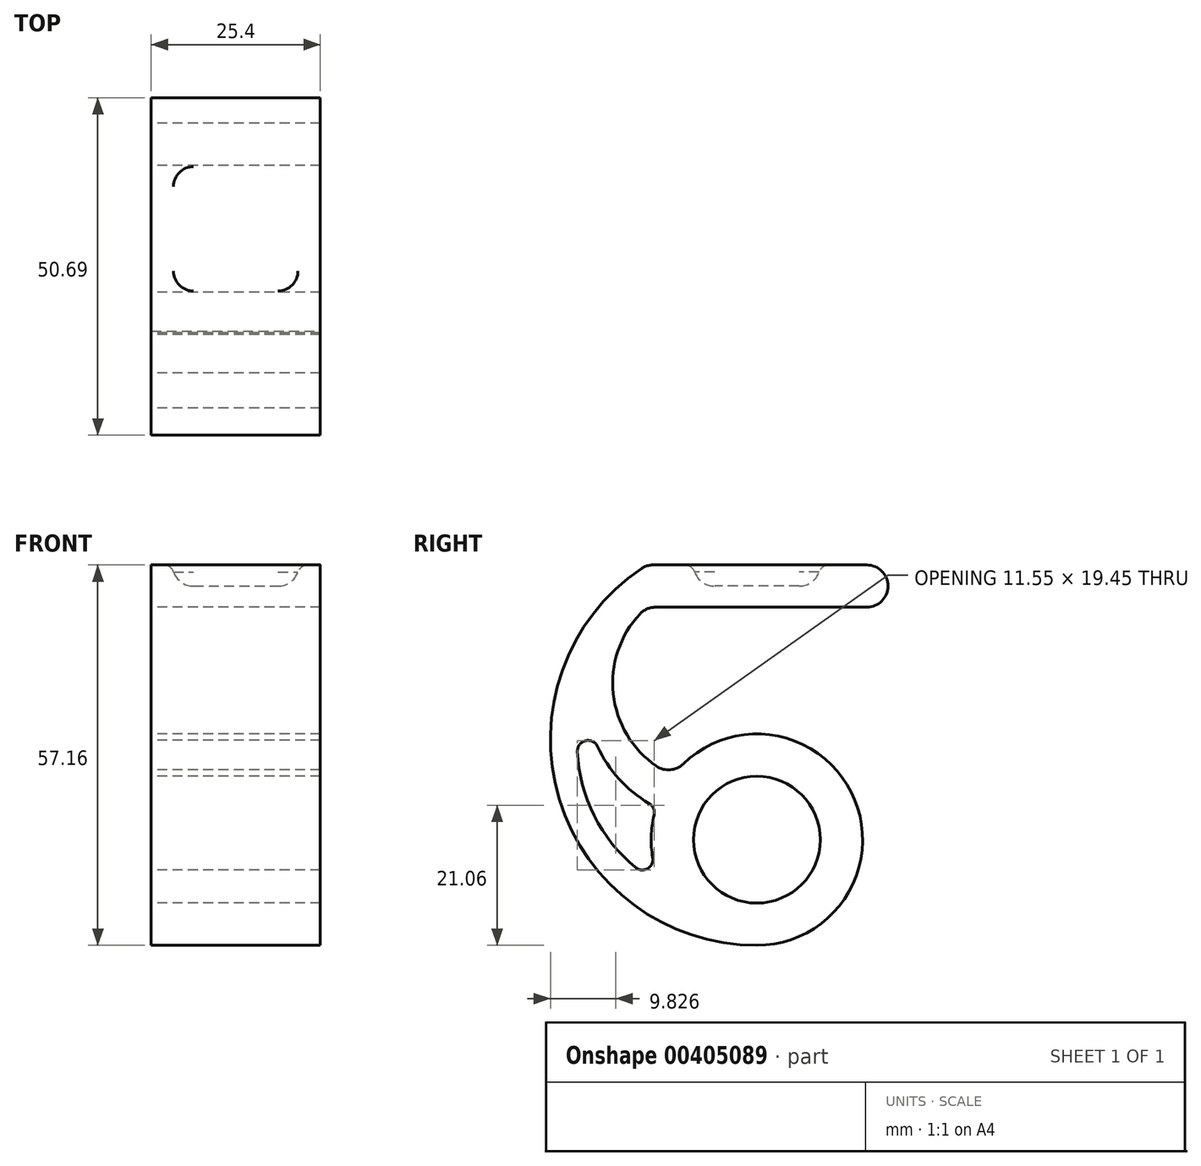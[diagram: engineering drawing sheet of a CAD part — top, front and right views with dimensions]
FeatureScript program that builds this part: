
annotation { "Feature Type Name" : "Feature", "Feature Type Description" : "" }
export const myFeature = defineFeature(function(context is Context, id is Id, definition is map)
    precondition{}
    {
        {
            var Q0;
            Q0=qCreatedBy(makeId("Right.planeOp"),FACE);
            var sketch = newSketch(context, id + "F0", { "sketchPlane" : qUnion([Q0])});
            skLineSegment(sketch, "E0.bottom", {"start": v(-16.51, 15.88) * mm, "end": v(16.51, 15.88) * mm});
            skLineSegment(sketch, "E0.top", {"start": v(-16.51, 9.53) * mm, "end": v(16.51, 9.53) * mm});
            skLineSegment(sketch, "E0.right", {"start": v(16.51, 15.88) * mm, "end": v(16.51, 9.53) * mm, "construction": true});
            skPoint(sketch, "E0.middle", {"position": v(0, 12.7) * mm});
            skLineSegment(sketch, "E1", {"start": v(-31.75, -9.53) * mm, "end": v(31.75, -9.53) * mm, "construction": true});
            skLineSegment(sketch, "E2", {"start": v(0, 9.53) * mm, "end": v(0, 0) * mm, "construction": true});
            skLineSegment(sketch, "E3", {"start": v(0, 0) * mm, "end": v(0, -9.53) * mm, "construction": true});
            skCircle(sketch, "E4", {"center": v(0, -25.4) * mm, "radius": 15.88 * mm, "construction": true});
            skArc(sketch, "E5", {"start": v(-16.51, 9.52) * mm, "mid": v(-21.47, -4.18) * mm, "end": v(-12.6, -15.74) * mm});
            skArc(sketch, "E6", {"start": v(16.51, 9.52) * mm, "mid": v(19.69, 12.7) * mm, "end": v(16.51, 15.88) * mm});
            skArc(sketch, "E7", {"start": v(-16.51, 15.87) * mm, "mid": v(-29.79, -18.92) * mm, "end": v(0, -41.28) * mm});
            skLineSegment(sketch, "E8", {"start": v(-12.6, -15.74) * mm, "end": v(0, -25.4) * mm, "construction": true});
            skLineSegment(sketch, "E9", {"start": v(0, -9.53) * mm, "end": v(0, -25.4) * mm, "construction": true});
            skArc(sketch, "E10", {"start": v(0, -41.27) * mm, "mid": v(14.24, -18.38) * mm, "end": v(-12.6, -15.74) * mm});
            skCircle(sketch, "E11", {"center": v(0, -25.4) * mm, "radius": 9.53 * mm});
            skArc(sketch, "E12", {"start": v(-25.68, -3.2) * mm, "mid": v(-22.87, -13.38) * mm, "end": v(-15.12, -20.55) * mm});
            skArc(sketch, "E13", {"start": v(-25.68, -3.2) * mm, "mid": v(-25.32, -19.77) * mm, "end": v(-14.34, -32.2) * mm});
            skArc(sketch, "E14", {"start": v(-15.12, -20.55) * mm, "mid": v(-15.84, -26.45) * mm, "end": v(-14.34, -32.2) * mm});
            skSolve(sketch);
        }
        {
            var Q0;
            Q0 = qSketchRegion(id + "F0", true);
            extrude(context, id + "F1", {"entities" : qUnion([Q0]), "depth" : 25.4 * mm, "offsetDistance" : 25.4 * mm});
        }
        {
            var Q0;
            Q0=makeQuery(id+"F1.opExtrude","SWEPT_FACE",FACE,{"disambiguationData":[OSD([sQuery(id+"F0.wireOp",EDGE,"E0.bottom")])]});
            var sketch = newSketch(context, id + "F2", { "sketchPlane" : qUnion([Q0])});
            skLineSegment(sketch, "E15.bottom", {"start": v(3.18, 9.52) * mm, "end": v(22.23, 9.53) * mm});
            skLineSegment(sketch, "E15.top", {"start": v(3.18, -9.53) * mm, "end": v(22.23, -9.53) * mm});
            skLineSegment(sketch, "E15.left", {"start": v(3.18, 9.52) * mm, "end": v(3.18, -9.53) * mm});
            skLineSegment(sketch, "E15.right", {"start": v(22.23, 9.53) * mm, "end": v(22.23, -9.52) * mm});
            skPoint(sketch, "E15.middle", {"position": v(12.7, 0) * mm});
            skLineSegment(sketch, "E16", {"start": v(12.7, 16.51) * mm, "end": v(12.7, 0) * mm, "construction": true});
            skSolve(sketch);
        }
        {
            var Q0;
            Q0 = qSketchRegion(id + "F2", true);
            extrude(context, id + "F3", {"entities" : qUnion([Q0]), "operationType" : NewBodyOperationType.REMOVE, "oppositeDirection" : true, "depth" : 3.17 * mm, "offsetDistance" : 25.4 * mm});
        }
        {
            var Q0;
            Q0=makeQuery(id+"F1.opExtrude","SWEPT_EDGE",EDGE,{"disambiguationData":[OSD([sQuery(id+"F0.wireOp",EDGE,"E5"),sQuery(id+"F0.wireOp",EDGE,"SAfVAtWe-y4kB-1YMZ-6q3z-Nys7H7JM4cN9")])]});
            var Q1;
            Q1=makeQuery(id+"F3.boolean.opBoolean","COPY",FACE,{"derivedFrom":makeQuery(id+"F3.opExtrude","CAP_FACE",FACE,{"disambiguationData":[OSD([sQuery(id+"F2.wireOp",EDGE,"E15.bottom"),sQuery(id+"F2.wireOp",EDGE,"E15.top"),sQuery(id+"F2.wireOp",EDGE,"E15.left"),sQuery(id+"F2.wireOp",EDGE,"E15.right")])],"isStart":false})});
            var Q2;
            Q2=makeQuery(id+"F3.boolean.opBoolean","COPY",EDGE,{"derivedFrom":makeQuery(id+"F3.opExtrude","SWEPT_EDGE",EDGE,{"disambiguationData":[OSD([sQuery(id+"F2.wireOp",EDGE,"E15.bottom"),sQuery(id+"F2.wireOp",EDGE,"E15.left")])]})});
            var Q3;
            Q3=makeQuery(id+"F3.boolean.opBoolean","COPY",EDGE,{"derivedFrom":makeQuery(id+"F3.opExtrude","SWEPT_EDGE",EDGE,{"disambiguationData":[OSD([sQuery(id+"F2.wireOp",EDGE,"E15.top"),sQuery(id+"F2.wireOp",EDGE,"E15.left")])]})});
            var Q4;
            Q4=makeQuery(id+"F3.boolean.opBoolean","COPY",EDGE,{"derivedFrom":makeQuery(id+"F3.opExtrude","SWEPT_EDGE",EDGE,{"disambiguationData":[OSD([sQuery(id+"F2.wireOp",EDGE,"E15.top"),sQuery(id+"F2.wireOp",EDGE,"E15.right")])]})});
            var Q5;
            Q5=makeQuery(id+"F3.boolean.opBoolean","COPY",EDGE,{"derivedFrom":makeQuery(id+"F3.opExtrude","SWEPT_EDGE",EDGE,{"disambiguationData":[OSD([sQuery(id+"F2.wireOp",EDGE,"E15.bottom"),sQuery(id+"F2.wireOp",EDGE,"E15.right")])]})});
            var Q6;
            Q6=makeQuery(id+"F1.opExtrude","SWEPT_EDGE",EDGE,{"disambiguationData":[OSD([sQuery(id+"F0.wireOp",EDGE,"E0.bottom"),sQuery(id+"F0.wireOp",EDGE,"E7")])]});
            fillet(context, id + "F4", {"entities" : qUnion([Q0, Q1, Q2, Q3, Q4, Q5, Q6]), "radius" : 3.17 * mm, "tangentPropagation" : true, "allowEdgeOverflow" : false});
        }
        {
            var Q0;
            Q0=makeQuery(id+"F4.opFillet","BLEND_EDGE",EDGE,{"blendedFrom":[makeQuery(id+"F3.boolean.opBoolean","COPY",EDGE,{"derivedFrom":makeQuery(id+"F3.opExtrude","CAP_EDGE",EDGE,{"disambiguationData":[OSD([sQuery(id+"F2.wireOp",EDGE,"E15.top")])],"isStart":false})}),makeQuery(id+"F1.opExtrude","SWEPT_FACE",FACE,{"disambiguationData":[OSD([sQuery(id+"F0.wireOp",EDGE,"E0.bottom")])]})],"blendedInto":[makeQuery(id+"F1.opExtrude","SWEPT_FACE",FACE,{"disambiguationData":[OSD([sQuery(id+"F0.wireOp",EDGE,"E0.bottom")])]})]});
            var Q1;
            Q1=makeQuery(id+"F4.opFillet","BLEND_EDGE",EDGE,{"blendedFrom":[makeQuery(id+"F3.boolean.opBoolean","COPY",VERTEX,{"derivedFrom":makeQuery(id+"F3.opExtrude","CAP_VERTEX",VERTEX,{"disambiguationData":[OSD([sQuery(id+"F2.wireOp",EDGE,"E15.top"),sQuery(id+"F2.wireOp",EDGE,"E15.left")])],"isStart":false})}),makeQuery(id+"F1.opExtrude","SWEPT_FACE",FACE,{"disambiguationData":[OSD([sQuery(id+"F0.wireOp",EDGE,"E0.bottom")])]})],"blendedInto":[makeQuery(id+"F1.opExtrude","SWEPT_FACE",FACE,{"disambiguationData":[OSD([sQuery(id+"F0.wireOp",EDGE,"E0.bottom")])]})]});
            var Q2;
            Q2=makeQuery(id+"F4.opFillet","BLEND_EDGE",EDGE,{"blendedFrom":[makeQuery(id+"F3.boolean.opBoolean","COPY",EDGE,{"derivedFrom":makeQuery(id+"F3.opExtrude","CAP_EDGE",EDGE,{"disambiguationData":[OSD([sQuery(id+"F2.wireOp",EDGE,"E15.left")])],"isStart":false})}),makeQuery(id+"F1.opExtrude","SWEPT_FACE",FACE,{"disambiguationData":[OSD([sQuery(id+"F0.wireOp",EDGE,"E0.bottom")])]})],"blendedInto":[makeQuery(id+"F1.opExtrude","SWEPT_FACE",FACE,{"disambiguationData":[OSD([sQuery(id+"F0.wireOp",EDGE,"E0.bottom")])]})]});
            var Q3;
            Q3=makeQuery(id+"F4.opFillet","BLEND_EDGE",EDGE,{"blendedFrom":[makeQuery(id+"F3.boolean.opBoolean","COPY",VERTEX,{"derivedFrom":makeQuery(id+"F3.opExtrude","CAP_VERTEX",VERTEX,{"disambiguationData":[OSD([sQuery(id+"F2.wireOp",EDGE,"E15.bottom"),sQuery(id+"F2.wireOp",EDGE,"E15.left")])],"isStart":false})}),makeQuery(id+"F1.opExtrude","SWEPT_FACE",FACE,{"disambiguationData":[OSD([sQuery(id+"F0.wireOp",EDGE,"E0.bottom")])]})],"blendedInto":[makeQuery(id+"F1.opExtrude","SWEPT_FACE",FACE,{"disambiguationData":[OSD([sQuery(id+"F0.wireOp",EDGE,"E0.bottom")])]})]});
            var Q4;
            Q4=makeQuery(id+"F4.opFillet","BLEND_EDGE",EDGE,{"blendedFrom":[makeQuery(id+"F3.boolean.opBoolean","COPY",EDGE,{"derivedFrom":makeQuery(id+"F3.opExtrude","CAP_EDGE",EDGE,{"disambiguationData":[OSD([sQuery(id+"F2.wireOp",EDGE,"E15.bottom")])],"isStart":false})}),makeQuery(id+"F1.opExtrude","SWEPT_FACE",FACE,{"disambiguationData":[OSD([sQuery(id+"F0.wireOp",EDGE,"E0.bottom")])]})],"blendedInto":[makeQuery(id+"F1.opExtrude","SWEPT_FACE",FACE,{"disambiguationData":[OSD([sQuery(id+"F0.wireOp",EDGE,"E0.bottom")])]})]});
            var Q5;
            Q5=makeQuery(id+"F4.opFillet","BLEND_EDGE",EDGE,{"blendedFrom":[makeQuery(id+"F3.boolean.opBoolean","COPY",VERTEX,{"derivedFrom":makeQuery(id+"F3.opExtrude","CAP_VERTEX",VERTEX,{"disambiguationData":[OSD([sQuery(id+"F2.wireOp",EDGE,"E15.bottom"),sQuery(id+"F2.wireOp",EDGE,"E15.right")])],"isStart":false})}),makeQuery(id+"F1.opExtrude","SWEPT_FACE",FACE,{"disambiguationData":[OSD([sQuery(id+"F0.wireOp",EDGE,"E0.bottom")])]})],"blendedInto":[makeQuery(id+"F1.opExtrude","SWEPT_FACE",FACE,{"disambiguationData":[OSD([sQuery(id+"F0.wireOp",EDGE,"E0.bottom")])]})]});
            var Q6;
            Q6=makeQuery(id+"F4.opFillet","BLEND_EDGE",EDGE,{"blendedFrom":[makeQuery(id+"F3.boolean.opBoolean","COPY",EDGE,{"derivedFrom":makeQuery(id+"F3.opExtrude","CAP_EDGE",EDGE,{"disambiguationData":[OSD([sQuery(id+"F2.wireOp",EDGE,"E15.right")])],"isStart":false})}),makeQuery(id+"F1.opExtrude","SWEPT_FACE",FACE,{"disambiguationData":[OSD([sQuery(id+"F0.wireOp",EDGE,"E0.bottom")])]})],"blendedInto":[makeQuery(id+"F1.opExtrude","SWEPT_FACE",FACE,{"disambiguationData":[OSD([sQuery(id+"F0.wireOp",EDGE,"E0.bottom")])]})]});
            var Q7;
            Q7=makeQuery(id+"F4.opFillet","BLEND_EDGE",EDGE,{"blendedFrom":[makeQuery(id+"F3.boolean.opBoolean","COPY",VERTEX,{"derivedFrom":makeQuery(id+"F3.opExtrude","CAP_VERTEX",VERTEX,{"disambiguationData":[OSD([sQuery(id+"F2.wireOp",EDGE,"E15.top"),sQuery(id+"F2.wireOp",EDGE,"E15.right")])],"isStart":false})}),makeQuery(id+"F1.opExtrude","SWEPT_FACE",FACE,{"disambiguationData":[OSD([sQuery(id+"F0.wireOp",EDGE,"E0.bottom")])]})],"blendedInto":[makeQuery(id+"F1.opExtrude","SWEPT_FACE",FACE,{"disambiguationData":[OSD([sQuery(id+"F0.wireOp",EDGE,"E0.bottom")])]})]});
            var Q8;
            Q8=makeQuery(id+"F1.opExtrude","SWEPT_EDGE",EDGE,{"disambiguationData":[OSD([sQuery(id+"F0.wireOp",EDGE,"E12"),sQuery(id+"F0.wireOp",EDGE,"E14")])]});
            var Q9;
            Q9=makeQuery(id+"F1.opExtrude","SWEPT_EDGE",EDGE,{"disambiguationData":[OSD([sQuery(id+"F0.wireOp",EDGE,"E13"),sQuery(id+"F0.wireOp",EDGE,"E14")])]});
            var Q10;
            Q10=makeQuery(id+"F1.opExtrude","SWEPT_EDGE",EDGE,{"disambiguationData":[OSD([sQuery(id+"F0.wireOp",EDGE,"E12"),sQuery(id+"F0.wireOp",EDGE,"E13")])]});
            fillet(context, id + "F5", {"entities" : qUnion([Q0, Q1, Q2, Q3, Q4, Q5, Q6, Q7, Q8, Q9, Q10]), "radius" : 1.59 * mm, "tangentPropagation" : true, "allowEdgeOverflow" : false});
        }
    });
